# Revit family: Grohe_ShowerHose_Silverflex_28362KF1
name_source: partatom
category: Plumbing Fixtures
units: mm (PartAtom-declared; Revit-internal decimal feet)

## family parameters
Cut with Voids When Loaded = No
Host = Face
OmniClass Number = 23.45.05.00
OmniClass Title = Sanitary Equipment
Part Type = Normal
Room Calculation Point = No
Round Connector Dimension = Use Diameter
Shared = No

## types (1)
- SILVERFLEX Shower Hose (28362KF1)
    Assembly Code = D2010
    AssetType = Fixed
    BIMObjectName = Grohe_ShowerHose_Silverflex_28362KF1
    CO2NeutralProduction = GROHE is one of the first leading manufacturer within the sanitary industry having a CO2-neutral production.
    CW Connection = No
    ClassificationName = Uniclass2015
    ClassificationValue = Pr_40_20_87_75
    Color = Matt Black
    Cost = 0 $
    Default Elevation = 0 mm  [stored 0 ft]
    Description = SILVERFLEX Shower Hose
    DimensionsDocumentLink = https://cdn.cloud.grohe.com
    DocumentationCertificates = https://www.bimstore.co
    DocumentationInstallationGuide = https://www.bimstore.co
    DocumentationLiterature = https://www.bimstore.co
    DocumentationMaintenance = https://www.bimstore.co
    DocumentationTechnical = https://www.bimstore.co
    DurationUnit = Years
    EF000007 = Other
    EF001438 = 1250 mm  [stored 4.10105 ft]
    EF005913 = not relevant
    EF013956 = FALSE
    EF022266 = Plastic
    EF022267 = TRUE
    EF022268 = Internal thread
    EF022269 = 1/2 inch
    EF024551 = not relevant
    Ecojoy = No
    ExpectedLife = 0
    FullRecyclabilityOfPlastic = All plastic components are fully recyclable
    GROHESocialCommittment = green.grohe.com/social_engagement
    GROHESustainability = green.grohe.com
    HW Connection = No
    HoseLength = 1250 mm  [stored 4.10105 ft]
    IfcExportAs = IfcPipeFitting
    IfcExportType = IfcPipeFittingType
    Keynote = N13
    Manufacturer = Grohe
    ManufacturerName = Grohe
    Model = SILVERFLEX Shower Hose
    ModelNumber = 28362KF1
    ModelReference = SILVERFLEX Shower Hose
    NBSDescription = Shower fittings package
    NBSObjectName = Grohe - Shower fittings package
    NBSReference = 45-35-70/330
    NominalDepth = 0 mm  [stored 0 ft]
    NominalHeight = 0 mm  [stored 0 ft]
    NominalLength = 0 mm  [stored 0 ft]
    PrimaryMaterial = Grohe_MattBlack
    ProductDescription = 1250 mm

plastic material with smooth surface

Extra Hygienic easy cleaning

AntiFold bendproof

universal connection G 1/2" x 1/2"

rotation cone for TwistStop-function

ProGrip

AntiScratch soft surface

GROHE Long-Life

heat resistance 70°C

pressure resistance up to 5 bar

tensile strength 500 N

GROHE Long-Life Shine finish
    ProductNumber = 28362KF1
    ProductPageURL = https://www.grohe.co.uk
    ProductShortText = shower hose 1250 mm
    ProductType = Shower Hose
    ProductionYear = 2023
    SustainabilityAward = green.grohe.com/awards
    SustainabilityReport = green.grohe.com/reporting
    Type Comments = SILVERFLEX Shower Hose
    TypeName = SILVERFLEX Shower Hose
    URL = https://www.grohe.co.uk
    Vent Connection = No
    WarrantyDurationLabor = 0
    WarrantyDurationParts = 0
    WarrantyDurationUnit = Years
    Waste Connection = No
    _BSBibleVersion = 17
    _BimSpecGuid = 0
    _CurrentRevision = 1
    _DistributedBy = https://www.bimstore.co
    _ObjectUserGuide = https://www.bimstore.co

note: [stored X ft] marks values corroborated as IEEE doubles in the binary element streams (Revit-internal decimal feet)

## geometry (parser evidence)
native form markers: Sweep x1
no freeform markers — native parametric forms only
